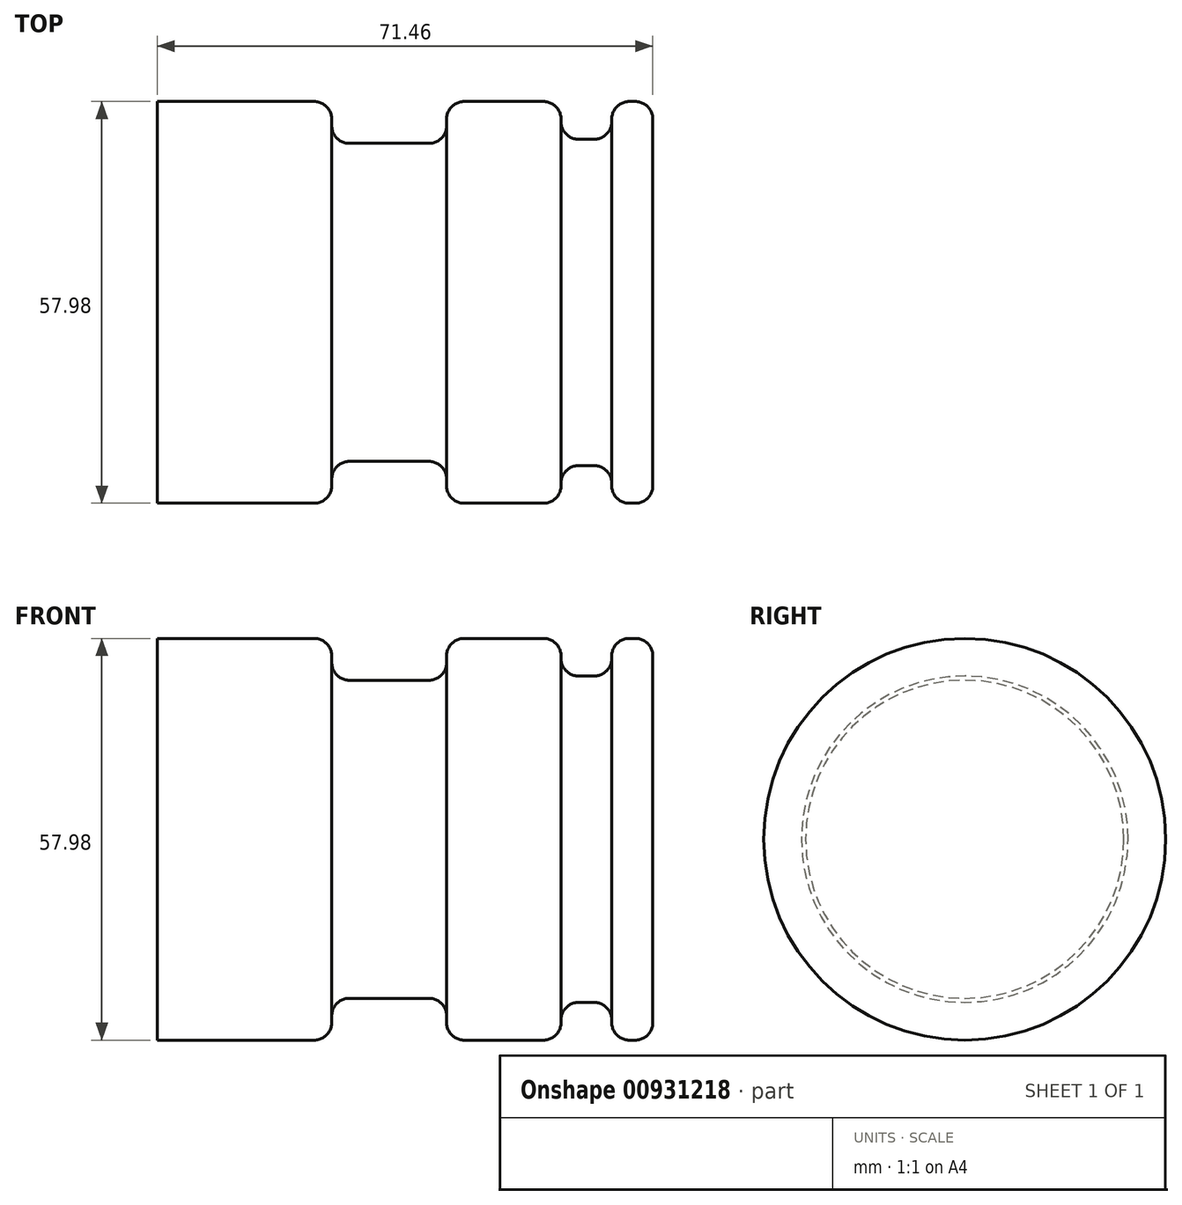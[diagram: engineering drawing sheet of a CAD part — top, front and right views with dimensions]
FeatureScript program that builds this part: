
annotation { "Feature Type Name" : "Feature", "Feature Type Description" : "" }
export const myFeature = defineFeature(function(context is Context, id is Id, definition is map)
    precondition{}
    {
        {
            var Q0;
            Q0=qCreatedBy(makeId("Front.planeOp"),FACE);
            var sketch = newSketch(context, id + "F0", { "sketchPlane" : qUnion([Q0])});
            skLineSegment(sketch, "E0.bottom", {"start": v(0, 0) * mm, "end": v(71.46, 0) * mm});
            skLineSegment(sketch, "E0.top", {"start": v(0, 29) * mm, "end": v(22.61, 29) * mm});
            skLineSegment(sketch, "E0.left", {"start": v(0, 0) * mm, "end": v(0, 29) * mm});
            skLineSegment(sketch, "E0.right", {"start": v(71.46, 0) * mm, "end": v(71.46, 26.45) * mm});
            skLineSegment(sketch, "E1", {"start": v(65.53, 26.45) * mm, "end": v(65.53, 26.09) * mm});
            skLineSegment(sketch, "E2", {"start": v(63, 23.55) * mm, "end": v(60.76, 23.55) * mm});
            skLineSegment(sketch, "E3", {"start": v(58.22, 26.09) * mm, "end": v(58.22, 26.45) * mm});
            skLineSegment(sketch, "E4", {"start": v(41.72, 26.45) * mm, "end": v(41.72, 25.5) * mm});
            skLineSegment(sketch, "E5", {"start": v(39.18, 22.95) * mm, "end": v(27.7, 22.95) * mm});
            skLineSegment(sketch, "E6", {"start": v(25.15, 25.5) * mm, "end": v(25.15, 26.45) * mm});
            skLineSegment(sketch, "E7.trimOffspring", {"start": v(44.26, 29) * mm, "end": v(55.68, 29) * mm});
            skLineSegment(sketch, "E8.trimOffspring", {"start": v(68.07, 29) * mm, "end": v(68.92, 29) * mm});
            skPoint(sketch, "E9.visualSharp", {"position": v(25.15, 29) * mm});
            skArc(sketch, "E9.filletArc", {"start": v(25.15, 26.45) * mm, "mid": v(24.41, 28.25) * mm, "end": v(22.61, 29) * mm});
            skPoint(sketch, "E10.visualSharp", {"position": v(25.15, 22.95) * mm});
            skArc(sketch, "E10.filletArc", {"start": v(25.15, 25.5) * mm, "mid": v(25.9, 23.7) * mm, "end": v(27.7, 22.95) * mm});
            skPoint(sketch, "E11.visualSharp", {"position": v(41.72, 22.95) * mm});
            skArc(sketch, "E11.filletArc", {"start": v(39.18, 22.95) * mm, "mid": v(40.98, 23.7) * mm, "end": v(41.72, 25.5) * mm});
            skPoint(sketch, "E12.visualSharp", {"position": v(41.72, 29) * mm});
            skArc(sketch, "E12.filletArc", {"start": v(44.26, 29) * mm, "mid": v(42.46, 28.25) * mm, "end": v(41.72, 26.45) * mm});
            skPoint(sketch, "E13.visualSharp", {"position": v(58.22, 29) * mm});
            skArc(sketch, "E13.filletArc", {"start": v(58.22, 26.45) * mm, "mid": v(57.47, 28.25) * mm, "end": v(55.68, 29) * mm});
            skPoint(sketch, "E14.visualSharp", {"position": v(58.22, 23.55) * mm});
            skArc(sketch, "E14.filletArc", {"start": v(58.22, 26.09) * mm, "mid": v(58.96, 24.3) * mm, "end": v(60.76, 23.55) * mm});
            skPoint(sketch, "E15.visualSharp", {"position": v(65.53, 23.55) * mm});
            skArc(sketch, "E15.filletArc", {"start": v(63, 23.55) * mm, "mid": v(64.79, 24.3) * mm, "end": v(65.53, 26.09) * mm});
            skPoint(sketch, "E16.visualSharp", {"position": v(65.53, 29) * mm});
            skArc(sketch, "E16.filletArc", {"start": v(68.07, 29) * mm, "mid": v(66.28, 28.25) * mm, "end": v(65.53, 26.45) * mm});
            skPoint(sketch, "E17.visualSharp", {"position": v(71.46, 29) * mm});
            skArc(sketch, "E17.filletArc", {"start": v(71.46, 26.45) * mm, "mid": v(70.72, 28.25) * mm, "end": v(68.92, 29) * mm});
            skSolve(sketch);
        }
        {
            var Q0;
            Q0=makeQuery(id+"F0.imprint","IMPRINT",FACE,{"disambiguationData":[TD([[makeQuery(id+"F0.imprint","IMPRINT",EDGE,{"derivedFrom":sQuery(id+"F0.wireOp",EDGE,"E0.bottom")}),1.0]])]});
            var Q1;
            Q1=sQuery(id+"F0.wireOp",EDGE,"E0.bottom");
            revolve(context, id + "F1", {"surfaceOperationType" : NewSurfaceOperationType.NEW, "entities" : qUnion([Q0]), "axis" : qUnion([Q1]), "revolveType" : RevolveType.FULL});
        }
    });
